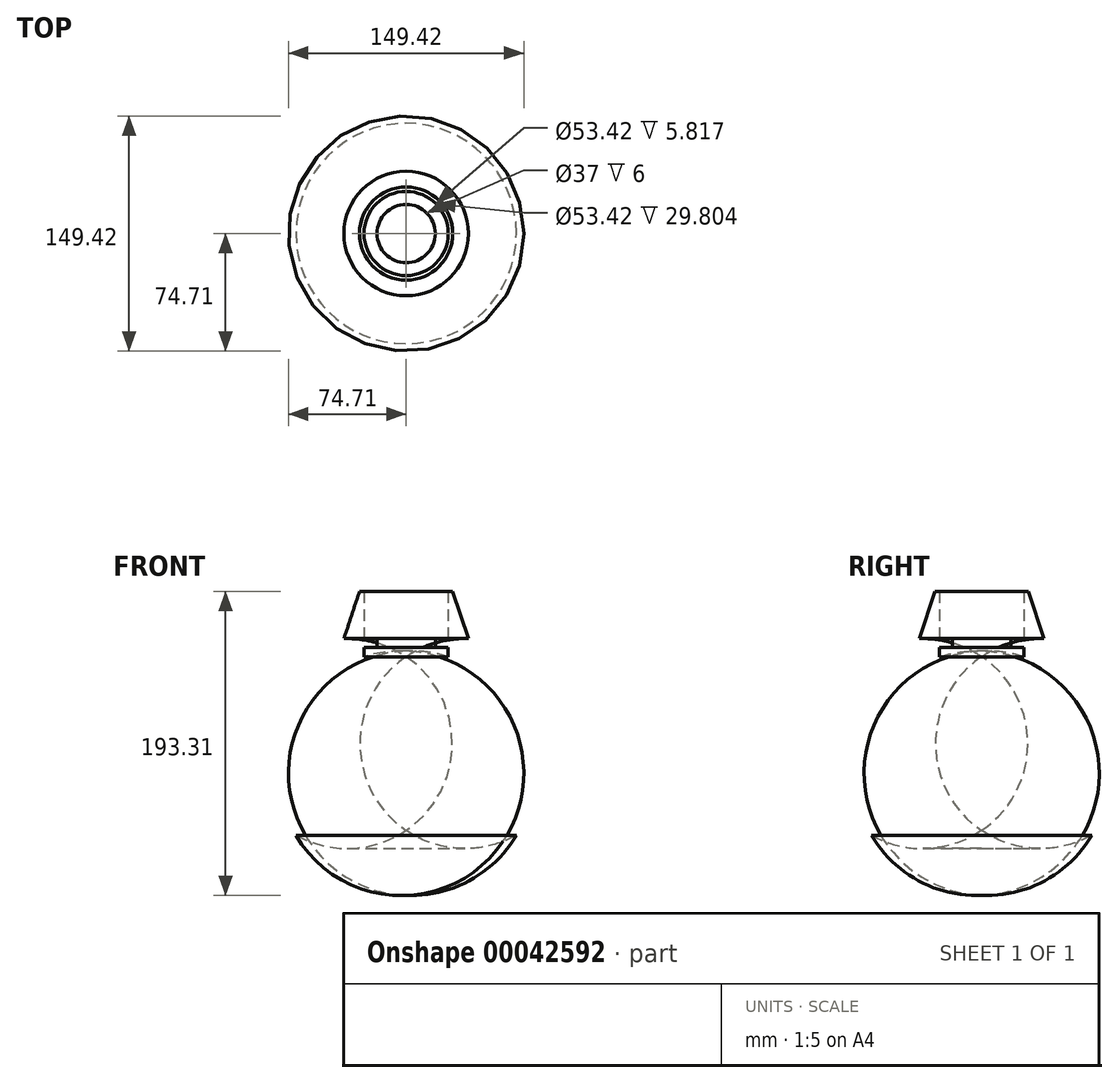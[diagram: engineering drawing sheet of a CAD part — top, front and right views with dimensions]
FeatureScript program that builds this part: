
annotation { "Feature Type Name" : "Feature", "Feature Type Description" : "" }
export const myFeature = defineFeature(function(context is Context, id is Id, definition is map)
    precondition{}
    {
        {
            var Q0;
            Q0=qCreatedBy(makeId("Front.planeOp"),FACE);
            var sketch = newSketch(context, id + "F0", { "sketchPlane" : qUnion([Q0])});
            skLineSegment(sketch, "E0", {"start": v(-26.71, 113.32) * mm, "end": v(-26.71, 119.13) * mm});
            skLineSegment(sketch, "E1", {"start": v(-26.71, 119.13) * mm, "end": v(-18.5, 119.13) * mm});
            skLineSegment(sketch, "E2", {"start": v(-18.5, 119.13) * mm, "end": v(-18.5, 125.13) * mm});
            skLineSegment(sketch, "E3", {"start": v(-18.5, 125.13) * mm, "end": v(-26.71, 125.13) * mm});
            skLineSegment(sketch, "E4", {"start": v(-26.71, 125.13) * mm, "end": v(-26.71, 154.94) * mm});
            skLineSegment(sketch, "E5", {"start": v(-26.71, 154.94) * mm, "end": v(-29.6, 154.94) * mm});
            skLineSegment(sketch, "E6", {"start": v(-29.6, 154.94) * mm, "end": v(-39.52, 124.85) * mm});
            skArc(sketch, "E7", {"start": v(-26.71, 113.32) * mm, "mid": v(-75.57, 67.06) * mm, "end": v(-70, 0) * mm});
            skArc(sketch, "E8", {"start": v(-39.52, 124.85) * mm, "mid": v(-102.18, 74) * mm, "end": v(-70, 0) * mm});
            skLineSegment(sketch, "E9", {"start": v(0, 0) * mm, "end": v(0, 163.6) * mm});
            skSolve(sketch);
        }
        {
            var Q0;
            Q0=makeQuery(id+"F0.imprint","IMPRINT",FACE,{"disambiguationData":[TD([[makeQuery(id+"F0.imprint","IMPRINT",EDGE,{"derivedFrom":sQuery(id+"F0.wireOp",EDGE,"E0")}),1.0]])]});
            var Q1;
            Q1=sQuery(id+"F0.wireOp",EDGE,"E9");
            revolve(context, id + "F1", {"entities" : qUnion([Q0]), "axis" : qUnion([Q1]), "revolveType" : RevolveType.FULL});
        }
    });
